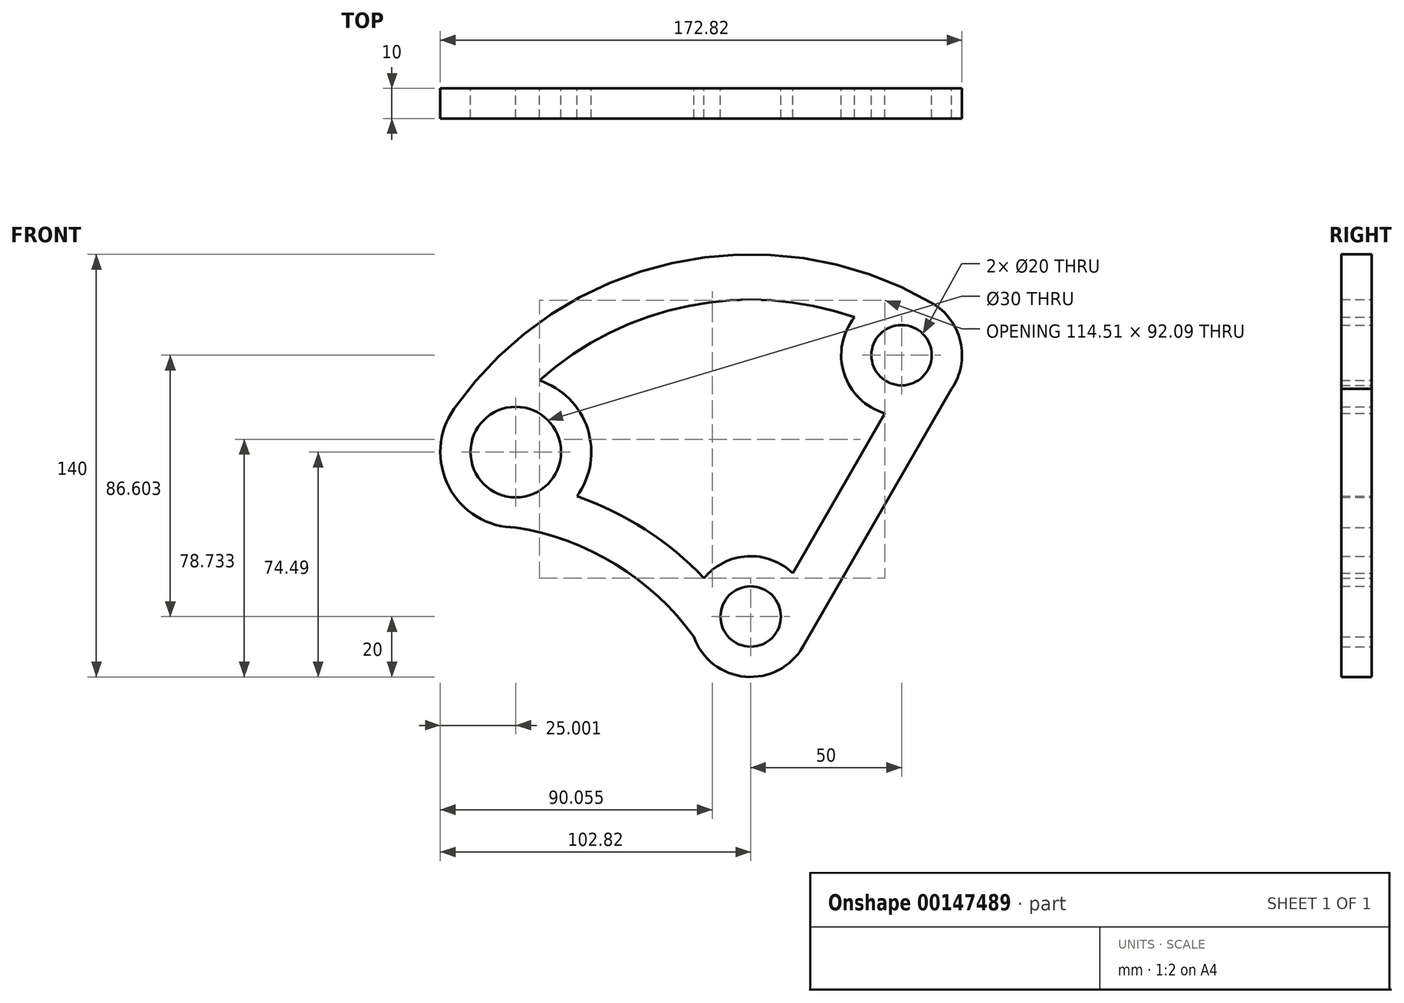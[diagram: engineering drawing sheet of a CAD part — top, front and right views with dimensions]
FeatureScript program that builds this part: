
annotation { "Feature Type Name" : "Feature", "Feature Type Description" : "" }
export const myFeature = defineFeature(function(context is Context, id is Id, definition is map)
    precondition{}
    {
        {
            var Q0;
            Q0=qCreatedBy(makeId("Front.planeOp"),FACE);
            var sketch = newSketch(context, id + "F0", { "sketchPlane" : qUnion([Q0])});
            skCircle(sketch, "E0", {"center": v(0, 0) * mm, "radius": 10 * mm});
            skArc(sketch, "E1", {"start": v(-18.84, -6.7) * mm, "mid": v(-0.73, -19.99) * mm, "end": v(18.3, -8.07) * mm});
            skArc(sketch, "E2", {"start": v(60, 103.92) * mm, "mid": v(-25.97, 117.16) * mm, "end": v(-98.3, 68.83) * mm});
            skCircle(sketch, "E3", {"center": v(50, 86.6) * mm, "radius": 10 * mm});
            skArc(sketch, "E4", {"start": v(65.9, 74.47) * mm, "mid": v(69.61, 90.53) * mm, "end": v(60, 103.92) * mm});
            skCircle(sketch, "E5", {"center": v(-77.82, 54.49) * mm, "radius": 15 * mm});
            skArc(sketch, "E6", {"start": v(-98.3, 68.83) * mm, "mid": v(-100, 42.95) * mm, "end": v(-77.82, 29.49) * mm});
            skLineSegment(sketch, "E7", {"start": v(17.32, -10) * mm, "end": v(66.58, 75.42) * mm});
            skArc(sketch, "E8", {"start": v(-18.84, -6.7) * mm, "mid": v(-44.71, 17.29) * mm, "end": v(-77.82, 29.49) * mm});
            skLineSegment(sketch, "E9.0", {"start": v(17.22, -9.94) * mm, "end": v(66.48, 75.48) * mm});
            skLineSegment(sketch, "E10.trimOffspring", {"start": v(-56.24, 39.38) * mm, "end": v(-57.34, 40.15) * mm});
            skArc(sketch, "E11.trimOffspring", {"start": v(-15.46, 12.69) * mm, "mid": v(-34.87, 28.81) * mm, "end": v(-57.56, 39.84) * mm});
            skLineSegment(sketch, "E12.trimOffspring", {"start": v(17.22, -9.94) * mm, "end": v(17.32, -10) * mm});
            skLineSegment(sketch, "E13.0", {"start": v(4.23, -2.45) * mm, "end": v(44.5, 67.38) * mm});
            skArc(sketch, "E14.trimOffspring", {"start": v(34.45, 99.19) * mm, "mid": v(-20.64, 102.95) * mm, "end": v(-70.02, 78.24) * mm});
            skArc(sketch, "E15.trimOffspring", {"start": v(-57.56, 39.84) * mm, "mid": v(-54.04, 62.2) * mm, "end": v(-70.02, 78.24) * mm});
            skArc(sketch, "E16.trimOffspring", {"start": v(13.92, 14.36) * mm, "mid": v(-1.14, 19.97) * mm, "end": v(-15.46, 12.69) * mm});
            skArc(sketch, "E17.trimOffspring", {"start": v(34.45, 99.19) * mm, "mid": v(30.93, 80.58) * mm, "end": v(44.5, 67.38) * mm});
            skSolve(sketch);
        }
        {
            var Q0;
            Q0 = qSketchRegion(id + "F0", true);
            extrude(context, id + "F1", {"entities" : qUnion([Q0]), "depth" : 10 * mm});
        }
    });
